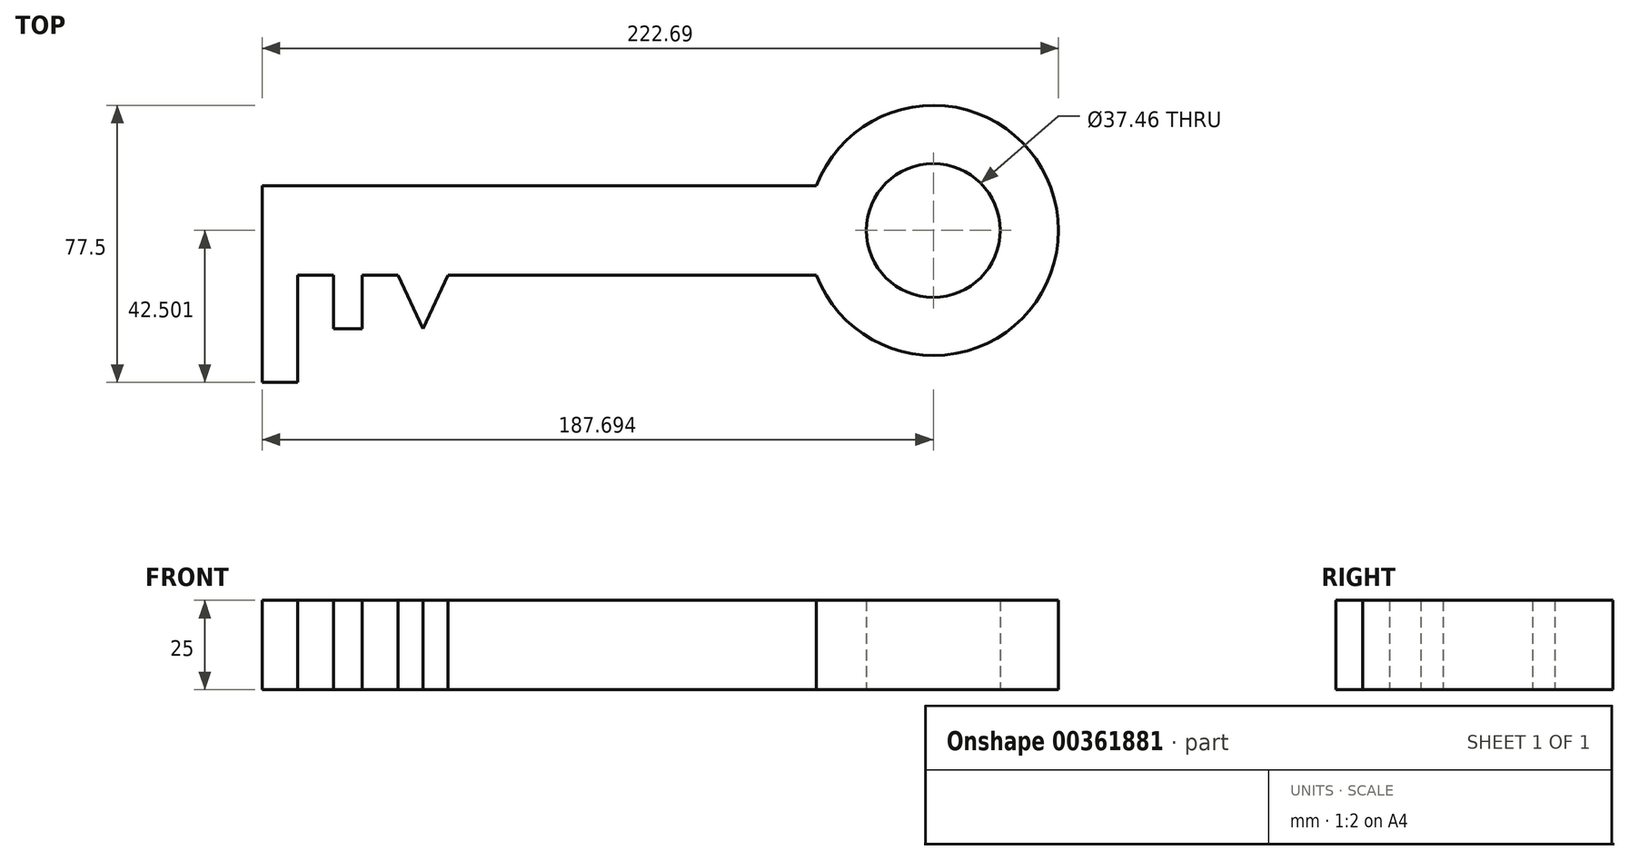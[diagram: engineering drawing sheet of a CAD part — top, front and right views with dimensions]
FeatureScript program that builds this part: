
annotation { "Feature Type Name" : "Feature", "Feature Type Description" : "" }
export const myFeature = defineFeature(function(context is Context, id is Id, definition is map)
    precondition{}
    {
        {
            var Q0;
            Q0=qCreatedBy(makeId("Top.planeOp"),FACE);
            var sketch = newSketch(context, id + "F0", { "sketchPlane" : qUnion([Q0])});
            skLineSegment(sketch, "E0.bottom", {"start": v(-79.23, 18.38) * mm, "end": v(75.77, 18.38) * mm});
            skLineSegment(sketch, "E0.top", {"start": v(-69.23, -6.62) * mm, "end": v(-59.23, -6.62) * mm});
            skLineSegment(sketch, "E0.left", {"start": v(-79.23, 18.38) * mm, "end": v(-79.23, -6.62) * mm});
            skLineSegment(sketch, "E1.top", {"start": v(-79.23, -36.62) * mm, "end": v(-69.23, -36.62) * mm});
            skLineSegment(sketch, "E1.left", {"start": v(-79.23, -6.62) * mm, "end": v(-79.23, -36.62) * mm});
            skLineSegment(sketch, "E1.right", {"start": v(-69.23, -6.62) * mm, "end": v(-69.23, -36.62) * mm});
            skLineSegment(sketch, "E2.top", {"start": v(-59.23, -21.62) * mm, "end": v(-51.23, -21.62) * mm});
            skLineSegment(sketch, "E2.left", {"start": v(-59.23, -6.62) * mm, "end": v(-59.23, -21.62) * mm});
            skLineSegment(sketch, "E2.right", {"start": v(-51.23, -6.62) * mm, "end": v(-51.23, -21.62) * mm});
            skPoint(sketch, "E3", {"position": v(-41.23, -6.62) * mm});
            skPoint(sketch, "E4", {"position": v(-34.23, -21.62) * mm});
            skPoint(sketch, "E5", {"position": v(-27.23, -6.62) * mm});
            skLineSegment(sketch, "E6", {"start": v(-41.23, -6.62) * mm, "end": v(-34.23, -21.62) * mm});
            skLineSegment(sketch, "E7", {"start": v(-34.23, -21.62) * mm, "end": v(-27.23, -6.62) * mm});
            skArc(sketch, "E8", {"start": v(75.77, -6.62) * mm, "mid": v(143.46, 5.88) * mm, "end": v(75.77, 18.38) * mm});
            skCircle(sketch, "E9", {"center": v(108.46, 5.88) * mm, "radius": 18.73 * mm});
            skLineSegment(sketch, "E10.trimOffspring", {"start": v(-27.23, -6.62) * mm, "end": v(75.77, -6.62) * mm});
            skLineSegment(sketch, "E11.trimOffspring", {"start": v(-51.23, -6.62) * mm, "end": v(-41.23, -6.62) * mm});
            skSolve(sketch);
        }
        {
            var Q0;
            Q0=makeQuery(id+"F0.imprint","IMPRINT",FACE,{"disambiguationData":[TD([[makeQuery(id+"F0.imprint","IMPRINT",EDGE,{"derivedFrom":sQuery(id+"F0.wireOp",EDGE,"E0.bottom")}),-1.0]])]});
            extrude(context, id + "F1", {"entities" : qUnion([Q0]), "depth" : 25 * mm});
        }
    });
